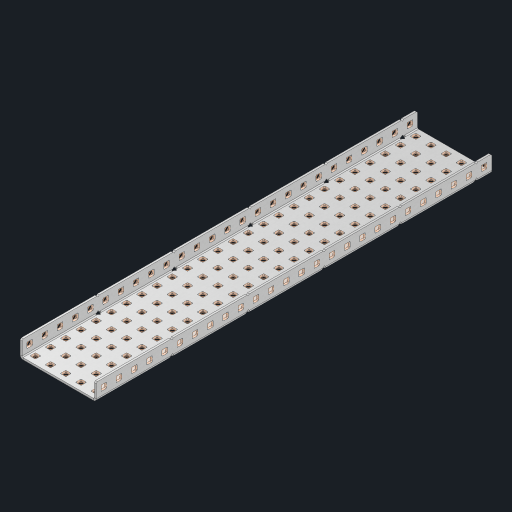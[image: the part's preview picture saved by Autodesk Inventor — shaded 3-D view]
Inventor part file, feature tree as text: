
AUTODESK INVENTOR PART (.ipt)
format: ipt  version: 2023 (Build 270158000, 158)  size: 2,046,464 bytes
history: native  units: in
note: dims shown in document units (in); Inventor stores cm internally (conversion verified against a paired STEP export)
features: other x187, extrude x181, sheet_metal_op x10, sketch x8, mirror x1, pattern_linear x1, chamfer x1
ambient origin geometry x8: Origin, YZ Plane, XZ Plane, XY Plane, X Axis, Y Axis, Z Axis, Center Point
bodies: Solid1 (feature_tree), Body (feature_tree)
feature tree (389):
  other  "Flange Pattern Plane"
  sheet_metal_op  "Flange Pattern"
  sheet_metal_op  "Body Pattern"
  other  "Arc Length"
  mirror  "Notch Mirror"
  pattern_linear  "Notch Pattern"  Spacing1=0.25in  [1 undecoded]
  chamfer  "End Chamfer"
  extrude  "Half Cut"  Depth=0.0625in
  sketch  "Sketch1"  dims[d0=2.5in]
  other  "Plate1"
  sketch  "Sketch2"  dims[d1=13.0in]
  other  "Plate2"
  sheet_metal_op  "Bend1"
  sheet_metal_op  "Corner1"
  sketch  "Sketch3"  dims[d2=0.0625in]
  other  "Flange Pattern Sketch"
  sketch  "Sketch7"  dims[d3=0.0625in]
  other  "Srf1"
  other  "Srf2"
  sketch  "Sketch8"  dims[d4=0.0312in]
  sketch  "Sketch9"  dims[d5=0.125in]
  other  "Srf91"
  sheet_metal_op  "Body Pattern Sketch"
  other  "Srf92"
  sketch  "Sketch13"  dims[d6=0.0625in]
  sketch  "Sketch14"  dims[d7=0.5in d8=90.0deg d9=0.0312in d10=0.25in d11=0.0625in d12=0.0625in d16=0.182in d17=0.02in d18=0.0625in d19=0.0in d20=0.25in d21=0.25in d46=0.172in d47=1.0in d48=0.0in d49=0.182in d50=0.02in d51=0.25in d52=0.25in d53=0.0625in d54=0.0in d55=0.172in d56=1.0in d57=0.0in d60=10.2362in d62=0.5in d63=1.9685in d65=0.5in d85=0.1473in d86=0.1782in d88=0.04in d89=0.0625in d90=0.0in d91=0.04in d92=0.0491in d95=2.5in d96=0.04in d97=0.25in d98=45.0deg d101=0.0in d102=2.497in d131=2.5in d132=10.2362in d134=0.5in d139=0.5in]
  other  "Srf856"
  other  "Srf1310"
  other  "Srf1311"
  other  "Srf1312"
  other  "Srf1376"
  other  "Srf1377"
  other  "Srf1728"
  other  "Srf1755"
  other  "Srf1878"
  other  "Srf1879"
  other  "Srf1880"
  other  "Srf1881"
  other  "Srf1882"
  other  "Srf1883"
  other  "Srf1884"
  other  "Srf1885"
  other  "Srf1886"
  other  "Srf1887"
  other  "Srf1888"
  other  "Srf1889"
  other  "Srf1890"
  other  "Srf1891"
  other  "Srf1892"
  other  "Srf1893"
  other  "Srf1894"
  other  "Srf1895"
  other  "Srf1896"
  other  "Srf1897"
  other  "Srf1898"
  other  "Srf1899"
  other  "Srf1900"
  other  "Srf1901"
  other  "Srf1902"
  other  "Srf1903"
  other  "Srf1904"
  other  "Srf1905"
  other  "Srf1906"
  other  "Srf1942"
  other  "Srf1943"
  other  "Srf1944"
  other  "Srf1945"
  other  "Srf1946"
  other  "Srf1947"
  other  "Srf1948"
  other  "Srf1949"
  other  "Srf1950"
  other  "Srf1951"
  other  "Srf1952"
  other  "Srf1953"
  other  "Srf1954"
  other  "Srf1955"
  other  "Srf1956"
  other  "Srf1957"
  other  "Srf1958"
  other  "Srf1959"
  other  "Srf1960"
  other  "Srf1961"
  other  "Srf1962"
  other  "Srf1963"
  other  "Srf1964"
  other  "Srf1965"
  other  "Srf1966"
  other  "Srf1967"
  other  "Srf1968"
  other  "Srf1969"
  other  "Srf1970"
  other  "Srf2111"
  other  "Srf2112"
  other  "Srf2113"
  other  "Srf2114"
  other  "Srf2115"
  other  "Srf2116"
  other  "Srf2117"
  other  "Srf2118"
  other  "Srf2119"
  other  "Srf2120"
  other  "Srf2121"
  other  "Srf2122"
  other  "Srf2123"
  other  "Srf2124"
  other  "Srf2125"
  other  "Srf2126"
  other  "Srf2127"
  other  "Srf2146"
  other  "Srf2147"
  other  "Srf2148"
  other  "Srf2149"
  other  "Srf2150"
  other  "Srf2151"
  other  "Srf2152"
  other  "Srf2153"
  other  "Srf2154"
  other  "Srf2155"
  other  "Srf2156"
  other  "Srf2157"
  other  "Srf2158"
  other  "Srf2159"
  other  "Srf2160"
  other  "Srf2161"
  other  "Srf2162"
  other  "Srf2163"
  other  "Srf2164"
  other  "Srf2165"
  other  "Srf2166"
  other  "Srf2167"
  other  "Srf2168"
  other  "Srf2169"
  other  "Srf2170"
  other  "Srf2171"
  other  "Srf2172"
  other  "Srf2173"
  other  "Srf2174"
  other  "Srf2175"
  other  "Srf2176"
  other  "Srf2177"
  other  "Srf2178"
  other  "Srf2179"
  other  "Srf2180"
  other  "Srf2181"
  other  "Srf2182"
  other  "Srf2183"
  other  "Srf2184"
  other  "Srf2185"
  other  "Srf2186"
  other  "Srf2187"
  other  "Srf2188"
  other  "Srf2189"
  other  "Srf2190"
  other  "Srf2191"
  other  "Srf2192"
  other  "Srf2193"
  other  "Srf2194"
  other  "Srf2195"
  other  "Srf2196"
  other  "Srf2197"
  other  "Srf2198"
  other  "Srf2199"
  other  "Srf2200"
  other  "Srf2201"
  other  "Srf2202"
  other  "Srf2203"
  other  "Srf2204"
  other  "Srf2205"
  other  "Srf2206"
  other  "Srf2207"
  other  "Srf2208"
  other  "Srf2209"
  other  "Srf2210"
  other  "Srf2211"
  other  "Srf2212"
  other  "Srf2213"
  other  "Srf2214"
  other  "Srf2215"
  other  "Srf2216"
  other  "Srf2217"
  other  "Srf2218"
  other  "Srf2219"
  other  "Srf2220"
  other  "Srf2221"
  other  "Srf2222"
  other  "Srf2223"
  other  "Srf2224"
  other  "Srf2225"
  other  "Srf2226"
  other  "Srf2227"
  other  "Srf2228"
  other  "Srf2229"
  other  "Srf2230"
  other  "Srf2231"
  other  "Srf2232"
  other  "Srf2233"
  other  "Srf2234"
  other  "Srf2235"
  other  "Srf2236"
  other  "Srf2237"
  other  "Srf2238"
  other  "Srf2239"
  other  "Srf2240"
  sheet_metal_op  "Flange Stamp"
  sheet_metal_op  "Flange Circle"
  sheet_metal_op  "Body Stamp"
  sheet_metal_op  "Body Circle"
  sheet_metal_op  "Notch"
  extrude  "ExtrusionSrf2"  Depth=0.0625in
  extrude  "ExtrusionSrf92"  Depth=2.5in
  extrude  "ExtrusionSrf856"  Depth=0.02in
  extrude  "ExtrusionSrf1310"  Depth=0.0625in
  extrude  "ExtrusionSrf1311"  TaperAngle=0.0deg  [1 undecoded]
  extrude  "ExtrusionSrf1312"  Depth=0.25in
  extrude  "ExtrusionSrf1376"  Depth=0.25in
  extrude  "ExtrusionSrf1377"  Depth=2.5in
  extrude  "ExtrusionSrf1728"  Depth=2.5in TaperAngle=0.0deg
  extrude  "ExtrusionSrf1755"  Depth=2.5in
  extrude  "ExtrusionSrf1878"  Depth=0.02in
  extrude  "ExtrusionSrf1879"  Depth=0.25in
  extrude  "ExtrusionSrf1880"  Depth=0.25in
  extrude  "ExtrusionSrf1881"  Depth=0.0625in
  extrude  "ExtrusionSrf1882"  TaperAngle=0.0deg  [1 undecoded]
  extrude  "ExtrusionSrf1883"  Depth=2.5in
  extrude  "ExtrusionSrf1884"  Depth=2.5in TaperAngle=0.0deg
  extrude  "ExtrusionSrf1885"  Depth=2.5in
  extrude  "ExtrusionSrf1886"  Depth=2.5in
  extrude  "ExtrusionSrf1887"  Depth=2.5in
  extrude  "ExtrusionSrf1888"  Depth=2.5in
  extrude  "ExtrusionSrf1889"  Depth=2.5in
  extrude  "ExtrusionSrf1890"  Depth=0.0625in
  extrude  "ExtrusionSrf1891"  TaperAngle=0.0deg  [1 undecoded]
  extrude  "ExtrusionSrf1892"  Depth=2.5in
  extrude  "ExtrusionSrf1893"  Depth=2.5in
  extrude  "ExtrusionSrf1894"  Depth=2.5in
  extrude  "ExtrusionSrf1895"  Depth=0.25in TaperAngle=45.0deg
  extrude  "ExtrusionSrf1896"  TaperAngle=0.0deg  [1 undecoded]
  extrude  "ExtrusionSrf1897"  Depth=2.5in
  extrude  "ExtrusionSrf1898"  Depth=2.5in
  extrude  "ExtrusionSrf1899"  Depth=2.5in
  extrude  "ExtrusionSrf1900"  Depth=2.5in
  extrude  "ExtrusionSrf1901"  Depth=2.5in
  extrude  "ExtrusionSrf1902"  [1 undecoded]
  extrude  "ExtrusionSrf1903"  [1 undecoded]
  extrude  "ExtrusionSrf1904"  [1 undecoded]
  extrude  "ExtrusionSrf1905"  [1 undecoded]
  extrude  "ExtrusionSrf1906"  [1 undecoded]
  extrude  "ExtrusionSrf1942"  [1 undecoded]
  extrude  "ExtrusionSrf1943"  [1 undecoded]
  extrude  "ExtrusionSrf1944"  [1 undecoded]
  extrude  "ExtrusionSrf1945"  [1 undecoded]
  extrude  "ExtrusionSrf1946"  [1 undecoded]
  extrude  "ExtrusionSrf1947"  [1 undecoded]
  extrude  "ExtrusionSrf1948"  [1 undecoded]
  extrude  "ExtrusionSrf1949"  [1 undecoded]
  extrude  "ExtrusionSrf1950"  [1 undecoded]
  extrude  "ExtrusionSrf1951"  [1 undecoded]
  extrude  "ExtrusionSrf1952"  [1 undecoded]
  extrude  "ExtrusionSrf1953"  [1 undecoded]
  extrude  "ExtrusionSrf1954"  [1 undecoded]
  extrude  "ExtrusionSrf1955"  [1 undecoded]
  extrude  "ExtrusionSrf1956"  [1 undecoded]
  extrude  "ExtrusionSrf1957"  [1 undecoded]
  extrude  "ExtrusionSrf1958"  [1 undecoded]
  extrude  "ExtrusionSrf1959"  [1 undecoded]
  extrude  "ExtrusionSrf1960"  [1 undecoded]
  extrude  "ExtrusionSrf1961"  [1 undecoded]
  extrude  "ExtrusionSrf1962"  [1 undecoded]
  extrude  "ExtrusionSrf1963"  [1 undecoded]
  extrude  "ExtrusionSrf1964"  [1 undecoded]
  extrude  "ExtrusionSrf1965"  [1 undecoded]
  extrude  "ExtrusionSrf1966"  [1 undecoded]
  extrude  "ExtrusionSrf1967"  [1 undecoded]
  extrude  "ExtrusionSrf1968"  [1 undecoded]
  extrude  "ExtrusionSrf1969"  [1 undecoded]
  extrude  "ExtrusionSrf1970"  [1 undecoded]
  extrude  "ExtrusionSrf2111"  [1 undecoded]
  extrude  "ExtrusionSrf2112"  [1 undecoded]
  extrude  "ExtrusionSrf2113"  [1 undecoded]
  extrude  "ExtrusionSrf2114"  [1 undecoded]
  extrude  "ExtrusionSrf2115"  [1 undecoded]
  extrude  "ExtrusionSrf2116"  [1 undecoded]
  extrude  "ExtrusionSrf2117"  [1 undecoded]
  extrude  "ExtrusionSrf2118"  [1 undecoded]
  extrude  "ExtrusionSrf2119"  [1 undecoded]
  extrude  "ExtrusionSrf2120"  [1 undecoded]
  extrude  "ExtrusionSrf2121"  [1 undecoded]
  extrude  "ExtrusionSrf2122"  [1 undecoded]
  extrude  "ExtrusionSrf2123"  [1 undecoded]
  extrude  "ExtrusionSrf2124"  [1 undecoded]
  extrude  "ExtrusionSrf2125"  [1 undecoded]
  extrude  "ExtrusionSrf2126"  [1 undecoded]
  extrude  "ExtrusionSrf2127"  [1 undecoded]
  extrude  "ExtrusionSrf2146"  [1 undecoded]
  extrude  "ExtrusionSrf2147"  [1 undecoded]
  extrude  "ExtrusionSrf2148"  [1 undecoded]
  extrude  "ExtrusionSrf2149"  [1 undecoded]
  extrude  "ExtrusionSrf2150"  [1 undecoded]
  extrude  "ExtrusionSrf2151"  [1 undecoded]
  extrude  "ExtrusionSrf2152"  [1 undecoded]
  extrude  "ExtrusionSrf2153"  [1 undecoded]
  extrude  "ExtrusionSrf2154"  [1 undecoded]
  extrude  "ExtrusionSrf2155"  [1 undecoded]
  extrude  "ExtrusionSrf2156"  [1 undecoded]
  extrude  "ExtrusionSrf2157"  [1 undecoded]
  extrude  "ExtrusionSrf2158"  [1 undecoded]
  extrude  "ExtrusionSrf2159"  [1 undecoded]
  extrude  "ExtrusionSrf2160"  [1 undecoded]
  extrude  "ExtrusionSrf2161"  [1 undecoded]
  extrude  "ExtrusionSrf2162"  [1 undecoded]
  extrude  "ExtrusionSrf2163"  [1 undecoded]
  extrude  "ExtrusionSrf2164"  [1 undecoded]
  extrude  "ExtrusionSrf2165"  [1 undecoded]
  extrude  "ExtrusionSrf2166"  [1 undecoded]
  extrude  "ExtrusionSrf2167"  [1 undecoded]
  extrude  "ExtrusionSrf2168"  [1 undecoded]
  extrude  "ExtrusionSrf2169"  [1 undecoded]
  extrude  "ExtrusionSrf2170"  [1 undecoded]
  extrude  "ExtrusionSrf2171"  [1 undecoded]
  extrude  "ExtrusionSrf2172"  [1 undecoded]
  extrude  "ExtrusionSrf2173"  [1 undecoded]
  extrude  "ExtrusionSrf2174"  [1 undecoded]
  extrude  "ExtrusionSrf2175"  [1 undecoded]
  extrude  "ExtrusionSrf2176"  [1 undecoded]
  extrude  "ExtrusionSrf2177"  [1 undecoded]
  extrude  "ExtrusionSrf2178"  [1 undecoded]
  extrude  "ExtrusionSrf2179"  [1 undecoded]
  extrude  "ExtrusionSrf2180"  [1 undecoded]
  extrude  "ExtrusionSrf2181"  [1 undecoded]
  extrude  "ExtrusionSrf2182"  [1 undecoded]
  extrude  "ExtrusionSrf2183"  [1 undecoded]
  extrude  "ExtrusionSrf2184"  [1 undecoded]
  extrude  "ExtrusionSrf2185"  [1 undecoded]
  extrude  "ExtrusionSrf2186"  [1 undecoded]
  extrude  "ExtrusionSrf2187"  [1 undecoded]
  extrude  "ExtrusionSrf2188"  [1 undecoded]
  extrude  "ExtrusionSrf2189"  [1 undecoded]
  extrude  "ExtrusionSrf2190"  [1 undecoded]
  extrude  "ExtrusionSrf2191"  [1 undecoded]
  extrude  "ExtrusionSrf2192"  [1 undecoded]
  extrude  "ExtrusionSrf2193"  [1 undecoded]
  extrude  "ExtrusionSrf2194"  [1 undecoded]
  extrude  "ExtrusionSrf2195"  [1 undecoded]
  extrude  "ExtrusionSrf2196"  [1 undecoded]
  extrude  "ExtrusionSrf2197"  [1 undecoded]
  extrude  "ExtrusionSrf2198"  [1 undecoded]
  extrude  "ExtrusionSrf2199"  [1 undecoded]
  extrude  "ExtrusionSrf2200"  [1 undecoded]
  extrude  "ExtrusionSrf2201"  [1 undecoded]
  extrude  "ExtrusionSrf2202"  [1 undecoded]
  extrude  "ExtrusionSrf2203"  [1 undecoded]
  extrude  "ExtrusionSrf2204"  [1 undecoded]
  extrude  "ExtrusionSrf2205"  [1 undecoded]
  extrude  "ExtrusionSrf2206"  [1 undecoded]
  extrude  "ExtrusionSrf2207"  [1 undecoded]
  extrude  "ExtrusionSrf2208"  [1 undecoded]
  extrude  "ExtrusionSrf2209"  [1 undecoded]
  extrude  "ExtrusionSrf2210"  [1 undecoded]
  extrude  "ExtrusionSrf2211"  [1 undecoded]
  extrude  "ExtrusionSrf2212"  [1 undecoded]
  extrude  "ExtrusionSrf2213"  [1 undecoded]
  extrude  "ExtrusionSrf2214"  [1 undecoded]
  extrude  "ExtrusionSrf2215"  [1 undecoded]
  extrude  "ExtrusionSrf2216"  [1 undecoded]
  extrude  "ExtrusionSrf2217"  [1 undecoded]
  extrude  "ExtrusionSrf2218"  [1 undecoded]
  extrude  "ExtrusionSrf2219"  [1 undecoded]
  extrude  "ExtrusionSrf2220"  [1 undecoded]
  extrude  "ExtrusionSrf2221"  [1 undecoded]
  extrude  "ExtrusionSrf2222"  [1 undecoded]
  extrude  "ExtrusionSrf2223"  [1 undecoded]
  extrude  "ExtrusionSrf2224"  [1 undecoded]
  extrude  "ExtrusionSrf2225"  [1 undecoded]
  extrude  "ExtrusionSrf2226"  [1 undecoded]
  extrude  "ExtrusionSrf2227"  [1 undecoded]
  extrude  "ExtrusionSrf2228"  [1 undecoded]
  extrude  "ExtrusionSrf2229"  [1 undecoded]
  extrude  "ExtrusionSrf2230"  [1 undecoded]
  extrude  "ExtrusionSrf2231"  [1 undecoded]
  extrude  "ExtrusionSrf2232"  [1 undecoded]
  extrude  "ExtrusionSrf2233"  [1 undecoded]
  extrude  "ExtrusionSrf2234"  [1 undecoded]
  extrude  "ExtrusionSrf2235"  [1 undecoded]
  extrude  "ExtrusionSrf2236"  [1 undecoded]
  extrude  "ExtrusionSrf2237"  [1 undecoded]
  extrude  "ExtrusionSrf2238"  [1 undecoded]
  extrude  "ExtrusionSrf2239"  [1 undecoded]
  extrude  "ExtrusionSrf2240"  [1 undecoded]
note: 151 required parameter values undecoded (feature->parameter linkage not recoverable at this tier; creation-order binding heuristic only, values carry confidence <= 0.55)
